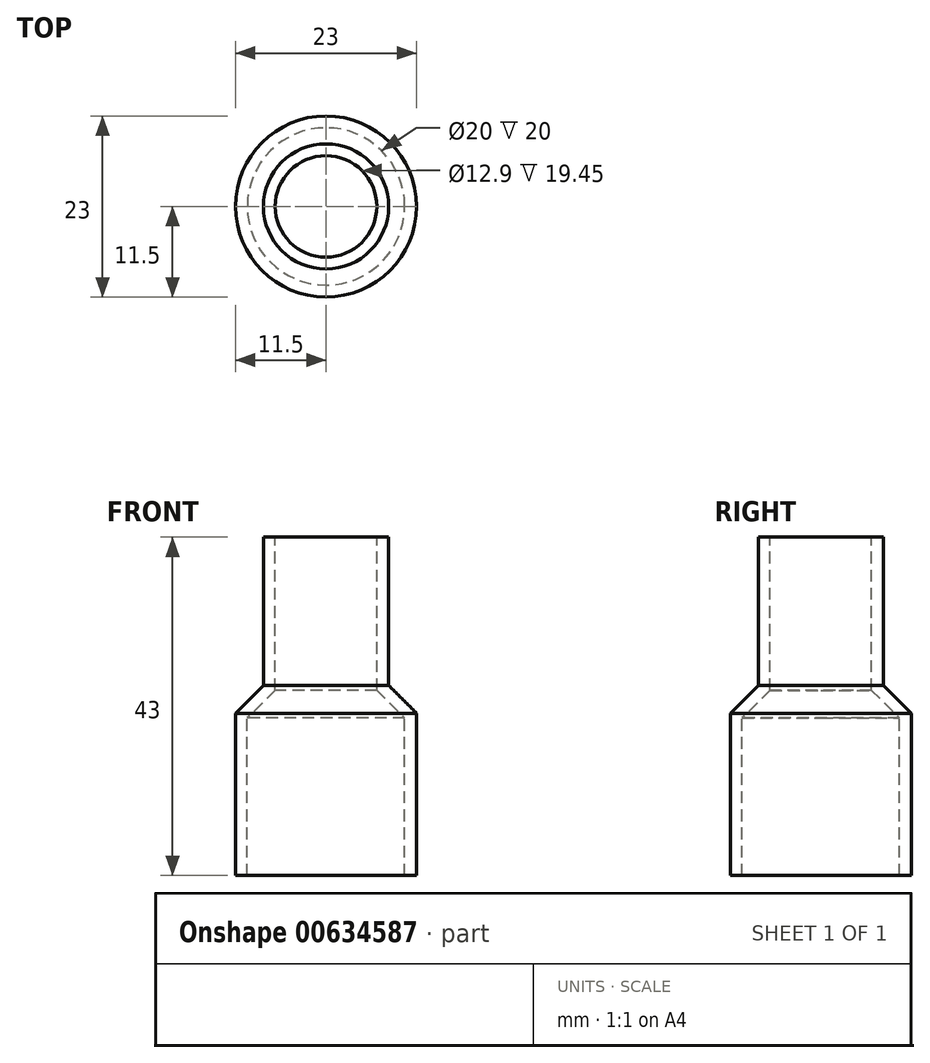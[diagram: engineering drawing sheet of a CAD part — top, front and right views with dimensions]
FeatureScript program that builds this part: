
annotation { "Feature Type Name" : "Feature", "Feature Type Description" : "" }
export const myFeature = defineFeature(function(context is Context, id is Id, definition is map)
    precondition{}
    {
        {
            var Q0;
            Q0=qCreatedBy(makeId("Front.planeOp"),FACE);
            var sketch = newSketch(context, id + "F0", { "sketchPlane" : qUnion([Q0])});
            skLineSegment(sketch, "E0", {"start": v(10, 0) * mm, "end": v(11.5, 0) * mm});
            skLineSegment(sketch, "E1", {"start": v(11.5, 0) * mm, "end": v(11.5, 20.62) * mm});
            skLineSegment(sketch, "E2", {"start": v(11.5, 20.62) * mm, "end": v(7.95, 24.17) * mm});
            skLineSegment(sketch, "E3", {"start": v(7.95, 24.17) * mm, "end": v(7.95, 43) * mm});
            skLineSegment(sketch, "E4", {"start": v(7.95, 43) * mm, "end": v(6.45, 43) * mm});
            skLineSegment(sketch, "E5", {"start": v(6.45, 43) * mm, "end": v(6.45, 23.55) * mm});
            skLineSegment(sketch, "E6", {"start": v(6.45, 23.55) * mm, "end": v(10, 20) * mm});
            skLineSegment(sketch, "E7", {"start": v(10, 20) * mm, "end": v(10, 0) * mm});
            skLineSegment(sketch, "E8", {"start": v(0, 49.07) * mm, "end": v(0, -5.19) * mm, "construction": true});
            skSolve(sketch);
        }
        {
            var Q0;
            Q0=makeQuery(id+"F0.imprint","IMPRINT",FACE,{"disambiguationData":[TD([[makeQuery(id+"F0.imprint","IMPRINT",EDGE,{"derivedFrom":sQuery(id+"F0.wireOp",EDGE,"E0")}),1.0]])]});
            var Q1;
            Q1=sQuery(id+"F0.wireOp",EDGE,"E8");
            revolve(context, id + "F1", {"entities" : qUnion([Q0]), "axis" : qUnion([Q1]), "revolveType" : RevolveType.FULL});
        }
    });
